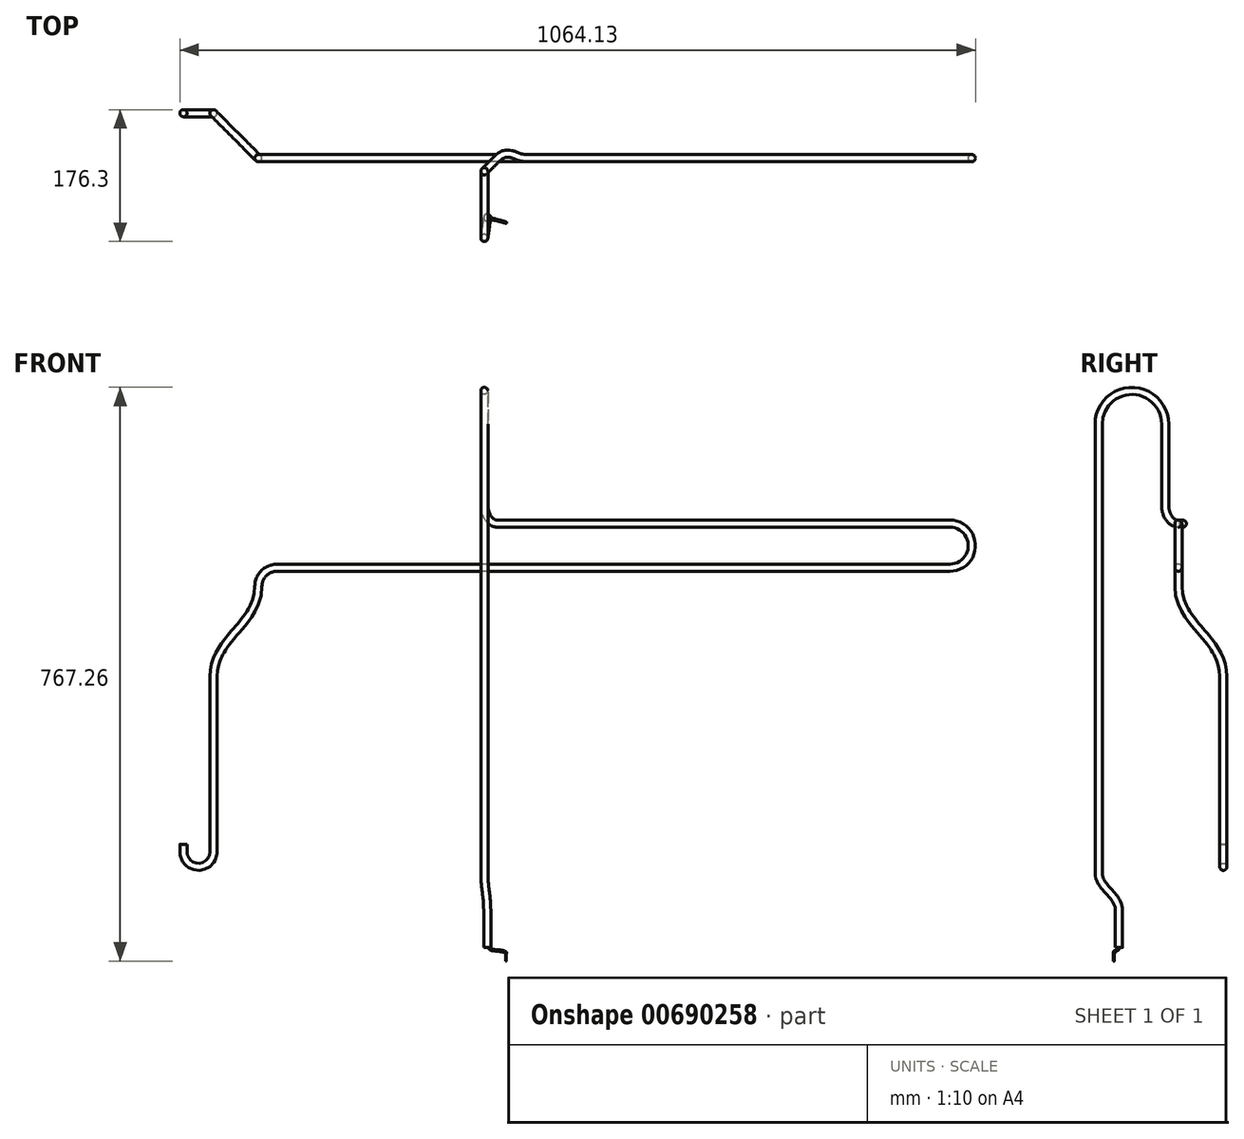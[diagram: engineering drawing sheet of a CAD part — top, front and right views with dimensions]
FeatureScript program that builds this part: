
annotation { "Feature Type Name" : "Feature", "Feature Type Description" : "" }
export const myFeature = defineFeature(function(context is Context, id is Id, definition is map)
    precondition{}
    {
        {
            var Q0;
            Q0=qCreatedBy(makeId("Top.planeOp"),FACE);
            var sketch = newSketch(context, id + "F0", { "sketchPlane" : qUnion([Q0])});
            skCircle(sketch, "E0", {"center": v(0, 0) * mm, "radius": 4.76 * mm});
            skSolve(sketch);
        }
        {
            var Q0;
            Q0=qCreatedBy(makeId("Right.planeOp"),FACE);
            var sketch = newSketch(context, id + "F1", { "sketchPlane" : qUnion([Q0])});
            skLineSegment(sketch, "E1", {"start": v(0, 50) * mm, "end": v(0, 0) * mm});
            skSolve(sketch);
        }
        {
            var Q0;
            Q0=sQuery(id+"F1.wireOp",EDGE,"E1");
            cPlane(context, id + "F2", {"entities" : qUnion([Q0]), "cplaneType" : CPlaneType.LINE_ANGLE, "offset" : 25 * mm, "angle" : 8 * degree, "width" : 150 * mm, "height" : 150 * mm});
        }
        {
            var Q0;
            Q0=qCreatedBy(id+"F2.planeOp",FACE);
            var sketch = newSketch(context, id + "F3", { "sketchPlane" : qUnion([Q0])});
            skFitSpline(sketch, "E2", {"points": [v(0, 50) * mm, v(13.75, 75) * mm, v(27.5, 100) * mm], "startDerivative": vector(0, 60) * mm, "endDerivative": vector(0, 60) * mm});
            skLineSegment(sketch, "E3", {"start": v(27.5, 90) * mm, "end": v(27.5, 100) * mm, "construction": true});
            skLineSegment(sketch, "E4", {"start": v(0, 60) * mm, "end": v(0, 50) * mm, "construction": true});
            skLineSegment(sketch, "E5", {"start": v(0, 50) * mm, "end": v(27.5, 100) * mm, "construction": true});
            skSolve(sketch);
        }
        {
            var Q0;
            Q0=qCreatedBy(makeId("Right.planeOp"),FACE);
            var Q1;
            Q1=sQuery(id+"F3.wireOp",VERTEX,"E2.2.internal");
            cPlane(context, id + "F4", {"entities" : qUnion([Q0, Q1]), "cplaneType" : CPlaneType.PLANE_POINT, "offset" : 25 * mm, "width" : 150 * mm, "height" : 150 * mm});
        }
        {
            var Q0;
            Q0=qCreatedBy(id+"F4.planeOp",FACE);
            var sketch = newSketch(context, id + "F5", { "sketchPlane" : qUnion([Q0])});
            skLineSegment(sketch, "E6", {"start": v(61.77, 592) * mm, "end": v(61.77, 700) * mm});
            skArc(sketch, "E7", {"start": v(61.77, 700) * mm, "mid": v(17.27, 744.5) * mm, "end": v(-27.23, 700) * mm});
            skLineSegment(sketch, "E8", {"start": v(-27.23, 100) * mm, "end": v(-27.23, 700) * mm});
            skSolve(sketch);
        }
        {
            var Q0;
            Q0=sQuery(id+"F5.wireOp",EDGE,"E6");
            cPlane(context, id + "F6", {"entities" : qUnion([Q0]), "cplaneType" : CPlaneType.LINE_ANGLE, "offset" : 25 * mm, "angle" : 45 * degree, "oppositeDirection" : true, "width" : 150 * mm, "height" : 150 * mm});
        }
        {
            var Q0;
            Q0=qCreatedBy(id+"F6.planeOp",FACE);
            var sketch = newSketch(context, id + "F7", { "sketchPlane" : qUnion([Q0])});
            skArc(sketch, "E9", {"start": v(40.97, 592) * mm, "mid": v(48.3, 574.32) * mm, "end": v(65.97, 567) * mm});
            skSolve(sketch);
        }
        {
            var Q0;
            Q0=qCreatedBy(makeId("Top.planeOp"),FACE);
            var Q1;
            Q1=sQuery(id+"F7.wireOp",VERTEX,"E9.end");
            cPlane(context, id + "F8", {"entities" : qUnion([Q0, Q1]), "cplaneType" : CPlaneType.PLANE_POINT, "offset" : 25 * mm, "width" : 150 * mm, "height" : 150 * mm});
        }
        {
            var Q0;
            Q0=qCreatedBy(id+"F8.planeOp",FACE);
            var sketch = newSketch(context, id + "F9", { "sketchPlane" : qUnion([Q0])});
            skFitSpline(sketch, "E10", {"points": [v(13.85, 79.45) * mm, v(33.85, 84.45) * mm, v(53.85, 79.45) * mm], "startDerivative": vector(42.43, 42.43) * mm, "endDerivative": vector(60, 0) * mm});
            skLineSegment(sketch, "E11", {"start": v(20.92, 86.52) * mm, "end": v(13.85, 79.45) * mm, "construction": true});
            skLineSegment(sketch, "E12", {"start": v(43.85, 79.45) * mm, "end": v(53.85, 79.45) * mm, "construction": true});
            skSolve(sketch);
        }
        {
            var Q0;
            Q0=qCreatedBy(makeId("Front.planeOp"),FACE);
            var Q1;
            Q1=sQuery(id+"F9.wireOp",VERTEX,"E12.end");
            cPlane(context, id + "F10", {"entities" : qUnion([Q0, Q1]), "cplaneType" : CPlaneType.PLANE_POINT, "offset" : 25 * mm, "width" : 150 * mm, "height" : 150 * mm});
        }
        {
            var Q0;
            Q0=qCreatedBy(id+"F10.planeOp",FACE);
            var sketch = newSketch(context, id + "F11", { "sketchPlane" : qUnion([Q0])});
            skLineSegment(sketch, "E13", {"start": v(53.85, 567) * mm, "end": v(618.85, 567) * mm});
            skArc(sketch, "E14", {"start": v(618.85, 508) * mm, "mid": v(648.35, 537.5) * mm, "end": v(618.85, 567) * mm});
            skLineSegment(sketch, "E15", {"start": v(618.85, 508) * mm, "end": v(-281.15, 508) * mm});
            skArc(sketch, "E16", {"start": v(-281.15, 508) * mm, "mid": v(-298.83, 500.68) * mm, "end": v(-306.15, 483) * mm});
            skLineSegment(sketch, "E17", {"start": v(-306.15, 483) * mm, "end": v(-306.15, 662.77) * mm, "construction": true});
            skSolve(sketch);
        }
        {
            var Q0;
            Q0=sQuery(id+"F11.wireOp",EDGE,"E17");
            cPlane(context, id + "F12", {"entities" : qUnion([Q0]), "cplaneType" : CPlaneType.LINE_ANGLE, "offset" : 25 * mm, "angle" : 45 * degree, "width" : 150 * mm, "height" : 150 * mm});
        }
        {
            var Q0;
            Q0=qCreatedBy(id+"F12.planeOp",FACE);
            var sketch = newSketch(context, id + "F13", { "sketchPlane" : qUnion([Q0])});
            skFitSpline(sketch, "E18", {"points": [v(272.66, 483) * mm, v(315.16, 423) * mm, v(357.66, 363) * mm], "startDerivative": vector(0, -150) * mm, "endDerivative": vector(0, -150) * mm});
            skLineSegment(sketch, "E19", {"start": v(272.66, 458) * mm, "end": v(272.66, 483) * mm, "construction": true});
            skLineSegment(sketch, "E20", {"start": v(357.66, 388) * mm, "end": v(357.66, 363) * mm, "construction": true});
            skLineSegment(sketch, "E21", {"start": v(357.66, 363) * mm, "end": v(272.66, 483) * mm, "construction": true});
            skSolve(sketch);
        }
        {
            var Q0;
            Q0=qCreatedBy(makeId("Front.planeOp"),FACE);
            var Q1;
            Q1=sQuery(id+"F13.wireOp",VERTEX,"E18.2.internal");
            cPlane(context, id + "F14", {"entities" : qUnion([Q0, Q1]), "cplaneType" : CPlaneType.PLANE_POINT, "offset" : 25 * mm, "width" : 150 * mm, "height" : 150 * mm});
        }
        {
            var Q0;
            Q0=qCreatedBy(id+"F14.planeOp",FACE);
            var sketch = newSketch(context, id + "F15", { "sketchPlane" : qUnion([Q0])});
            skLineSegment(sketch, "E22", {"start": v(-366.25, 128) * mm, "end": v(-366.25, 363) * mm});
            skArc(sketch, "E23", {"start": v(-406.25, 128) * mm, "mid": v(-386.25, 108) * mm, "end": v(-366.25, 128) * mm});
            skLineSegment(sketch, "E24", {"start": v(-406.25, 128) * mm, "end": v(-406.25, 138) * mm});
            skSolve(sketch);
        }
        {
            var Q0;
            Q0=qSketchRegion(id+"F0",true);
            var Q1;
            Q1=qConstructionFilter(qBodyType(qCreatedBy(id+"F1",EDGE),BodyType.WIRE),ConstructionObject.NO);
            var Q2;
            Q2=qConstructionFilter(qBodyType(qCreatedBy(id+"F3",EDGE),BodyType.WIRE),ConstructionObject.NO);
            var Q3;
            Q3=qConstructionFilter(qBodyType(qCreatedBy(id+"F5",EDGE),BodyType.WIRE),ConstructionObject.NO);
            var Q4;
            Q4=qConstructionFilter(qBodyType(qCreatedBy(id+"F7",EDGE),BodyType.WIRE),ConstructionObject.NO);
            var Q5;
            Q5=qConstructionFilter(qBodyType(qCreatedBy(id+"F9",EDGE),BodyType.WIRE),ConstructionObject.NO);
            var Q6;
            Q6=qConstructionFilter(qBodyType(qCreatedBy(id+"F11",EDGE),BodyType.WIRE),ConstructionObject.NO);
            var Q7;
            Q7=qConstructionFilter(qBodyType(qCreatedBy(id+"F13",EDGE),BodyType.WIRE),ConstructionObject.NO);
            var Q8;
            Q8=qConstructionFilter(qBodyType(qCreatedBy(id+"F15",EDGE),BodyType.WIRE),ConstructionObject.NO);
            sweep(context, id + "F16", {"profiles" : qUnion([Q0]), "path" : qUnion([Q1, Q2, Q3, Q4, Q5, Q6, Q7, Q8])});
        }
        {
            var Q0;
            Q0=makeQuery(id+"F16.opSweep","CAP_FACE",FACE,{"disambiguationData":[OSD([sQuery(id+"F0.wireOp",EDGE,"E0"),sQuery(id+"F1.wireOp",VERTEX,"9avbEkqO-CQ4f-H5Hg-38DB-rcSkPiFHVGC0.start")])],"isStart":true});
            var sketch = newSketch(context, id + "F17", { "sketchPlane" : qUnion([Q0])});
            skCircle(sketch, "E25", {"center": v(2.9, 0.78) * mm, "radius": 1 * mm});
            skLineSegment(sketch, "E26", {"start": v(0, 0) * mm, "end": v(4.76, 0) * mm, "construction": true});
            skLineSegment(sketch, "E27", {"start": v(0, 0) * mm, "end": v(4.6, 1.23) * mm, "construction": true});
            skSolve(sketch);
        }
        {
            var Q0;
            Q0=sQuery(id+"F17.wireOp",VERTEX,"E25.center");
            var Q1;
            Q1=sQuery(id+"F17.wireOp",VERTEX,"E27.start");
            var Q2;
            Q2=sQuery(id+"F1.wireOp",VERTEX,"E1.start");
            cPlane(context, id + "F18", {"entities" : qUnion([Q0, Q1, Q2]), "cplaneType" : CPlaneType.THREE_POINT, "offset" : 25 * mm, "width" : 150 * mm, "height" : 150 * mm});
        }
        {
            var Q0;
            Q0=qCreatedBy(id+"F18.planeOp",FACE);
            var sketch = newSketch(context, id + "F19", { "sketchPlane" : qUnion([Q0])});
            skFitSpline(sketch, "E28", {"points": [v(3, 0) * mm, v(14.5, -4) * mm, v(26, -8) * mm], "startDerivative": vector(0, -18) * mm, "endDerivative": vector(0, -18) * mm});
            skLineSegment(sketch, "E29", {"start": v(3, 0) * mm, "end": v(26, -8) * mm, "construction": true});
            skLineSegment(sketch, "E30", {"start": v(26, -5) * mm, "end": v(26, -8) * mm, "construction": true});
            skLineSegment(sketch, "E31", {"start": v(3, -3) * mm, "end": v(3, 0) * mm, "construction": true});
            skSolve(sketch);
        }
        {
            var Q0;
            Q0=qSketchRegion(id+"F17",true);
            var Q1;
            Q1=qConstructionFilter(qBodyType(qCreatedBy(id+"F19",EDGE),BodyType.WIRE),ConstructionObject.NO);
            sweep(context, id + "F20", {"operationType" : NewBodyOperationType.ADD, "profiles" : qUnion([Q0]), "path" : qUnion([Q1])});
        }
        {
            var Q0;
            Q0=makeQuery(id+"F20.opSweep","CAP_FACE",FACE,{"disambiguationData":[OSD([sQuery(id+"F17.wireOp",EDGE,"E25"),sQuery(id+"F19.wireOp",VERTEX,"E28.end")])],"isStart":false});
            var sketch = newSketch(context, id + "F21", { "sketchPlane" : qUnion([Q0])});
            skCircle(sketch, "E32", {"center": v(25.11, 6.73) * mm, "radius": 0.5 * mm});
            skSolve(sketch);
        }
        {
            var Q0;
            Q0=qSketchRegion(id+"F21",true);
            extrude(context, id + "F22", {"entities" : qUnion([Q0]), "operationType" : NewBodyOperationType.ADD, "depth" : 10 * mm});
        }
    });
